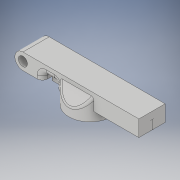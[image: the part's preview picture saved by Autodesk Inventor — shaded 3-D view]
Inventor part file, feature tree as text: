
AUTODESK INVENTOR PART (.ipt)
format: ipt  version: 2019 (Build 230136000, 136)  size: 349,696 bytes
history: native  units: in
note: dims shown in document units (in); Inventor stores cm internally (conversion verified against a paired STEP export)
features: extrude x7, sketch x7, fillet x6, chamfer x2
ambient origin geometry x8: Origin, YZ Plane, XZ Plane, XY Plane, X Axis, Y Axis, Z Axis, Center Point
bodies: Solid1 (feature_tree)
feature tree (22):
  extrude  "Extrusion1"  Depth=2.5709in
  extrude  "Extrusion2"  Depth=0.5827in TaperAngle=0.0deg
  extrude  "Extrusion3"  Depth=0.1969in TaperAngle=0.0deg
  chamfer  "Chamfer3"  Distance=0.1969in
  chamfer  "Chamfer4"  Distance=1.378in
  fillet  "Fillet4"  Radius=0.5827in
  fillet  "Fillet5"  Radius=0.2756in
  extrude  "Extrusion6"  Depth=0.1811in TaperAngle=120.0deg
  extrude  "Extrusion7"  Depth=0.0787in
  extrude  "Extrusion8"  Depth=0.0787in
  extrude  "Extrusion9"  Depth=0.8661in
  fillet  "Fillet6"  Radius=0.0394in
  fillet  "Fillet7"  Radius=0.5827in
  fillet  "Fillet8"  Radius=0.2913in
  fillet  "Fillet9"  Radius=0.0787in
  sketch  "Sketch1"  dims[d0=0.2008in d2=2.5709in]
  sketch  "Sketch2"  dims[d3=0.1791in d4=0.5827in d5=0.0in]
  sketch  "Sketch3"  dims[d6=0.5118in d7=0.1969in d8=0.0in]
  sketch  "Sketch10"  dims[d9=2.315in]
  sketch  "Sketch11"  dims[d11=0.9449in d13=0.1969in d14=0.0in]
  sketch  "Sketch12"  dims[d15=0.2913in]
  sketch  "Sketch13"  dims[d16=0.2913in d30=1.378in d45=0.5827in d46=0.2756in d47=0.1811in d48=120.0deg d49=0.1811in d50=0.2756in d51=120.0deg d52=0.0787in d53=0.0787in d54=0.8661in d55=0.0394in d56=0.0in d57=0.5827in d58=0.2913in d63=0.0787in d64=0.0394in d65=0.5827in d66=0.0in d67=0.1575in d68=0.5827in d69=0.2126in d70=0.2362in d71=0.0in d72=0.0787in d73=0.1575in d74=0.0787in d75=0.0787in d76=0.1575in d77=0.0in d78=0.1181in d79=0.0394in d80=0.0394in d81=0.0394in]
